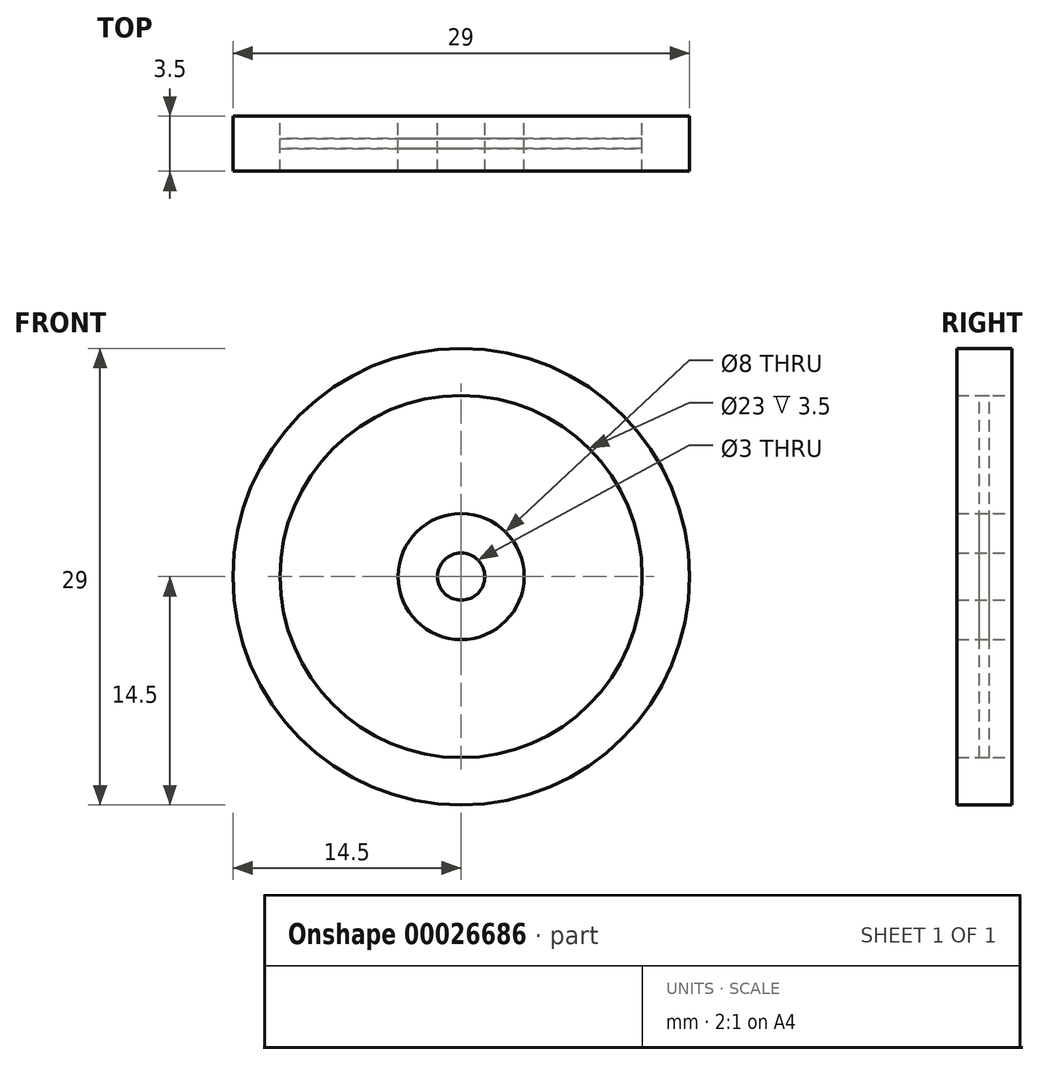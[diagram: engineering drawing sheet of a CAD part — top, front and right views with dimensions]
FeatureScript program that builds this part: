
annotation { "Feature Type Name" : "Feature", "Feature Type Description" : "" }
export const myFeature = defineFeature(function(context is Context, id is Id, definition is map)
    precondition{}
    {
        {
            var Q0;
            Q0=qCreatedBy(makeId("Front.planeOp"),FACE);
            var sketch = newSketch(context, id + "F0", { "sketchPlane" : qUnion([Q0])});
            skCircle(sketch, "E0", {"center": v(0, 0) * mm, "radius": 14.5 * mm});
            skCircle(sketch, "E1", {"center": v(0, 0) * mm, "radius": 4 * mm});
            skCircle(sketch, "E2", {"center": v(0, 0) * mm, "radius": 1.5 * mm});
            skCircle(sketch, "E3", {"center": v(0, 0) * mm, "radius": 11.5 * mm});
            skSolve(sketch);
        }
        {
            var Q0;
            Q0=makeQuery(id+"F0.imprint","IMPRINT",FACE,{"disambiguationData":[TD([[makeQuery(id+"F0.imprint","IMPRINT",EDGE,{"derivedFrom":sQuery(id+"F0.wireOp",EDGE,"E1")}),1.0]])]});
            var Q1;
            Q1=makeQuery(id+"F0.imprint","IMPRINT",FACE,{"disambiguationData":[TD([[makeQuery(id+"F0.imprint","IMPRINT",EDGE,{"derivedFrom":sQuery(id+"F0.wireOp",EDGE,"E0")}),1.0]])]});
            extrude(context, id + "F1", {"entities" : qUnion([Q0, Q1]), "endBound" : BoundingType.SYMMETRIC, "depth" : 3.5 * mm});
        }
        {
            var Q0;
            Q0=makeQuery(id+"F0.imprint","IMPRINT",FACE,{"disambiguationData":[TD([[makeQuery(id+"F0.imprint","IMPRINT",EDGE,{"derivedFrom":sQuery(id+"F0.wireOp",EDGE,"E1")}),-1.0]])]});
            extrude(context, id + "F2", {"entities" : qUnion([Q0]), "endBound" : BoundingType.SYMMETRIC, "depth" : .65 * mm});
        }
    });
